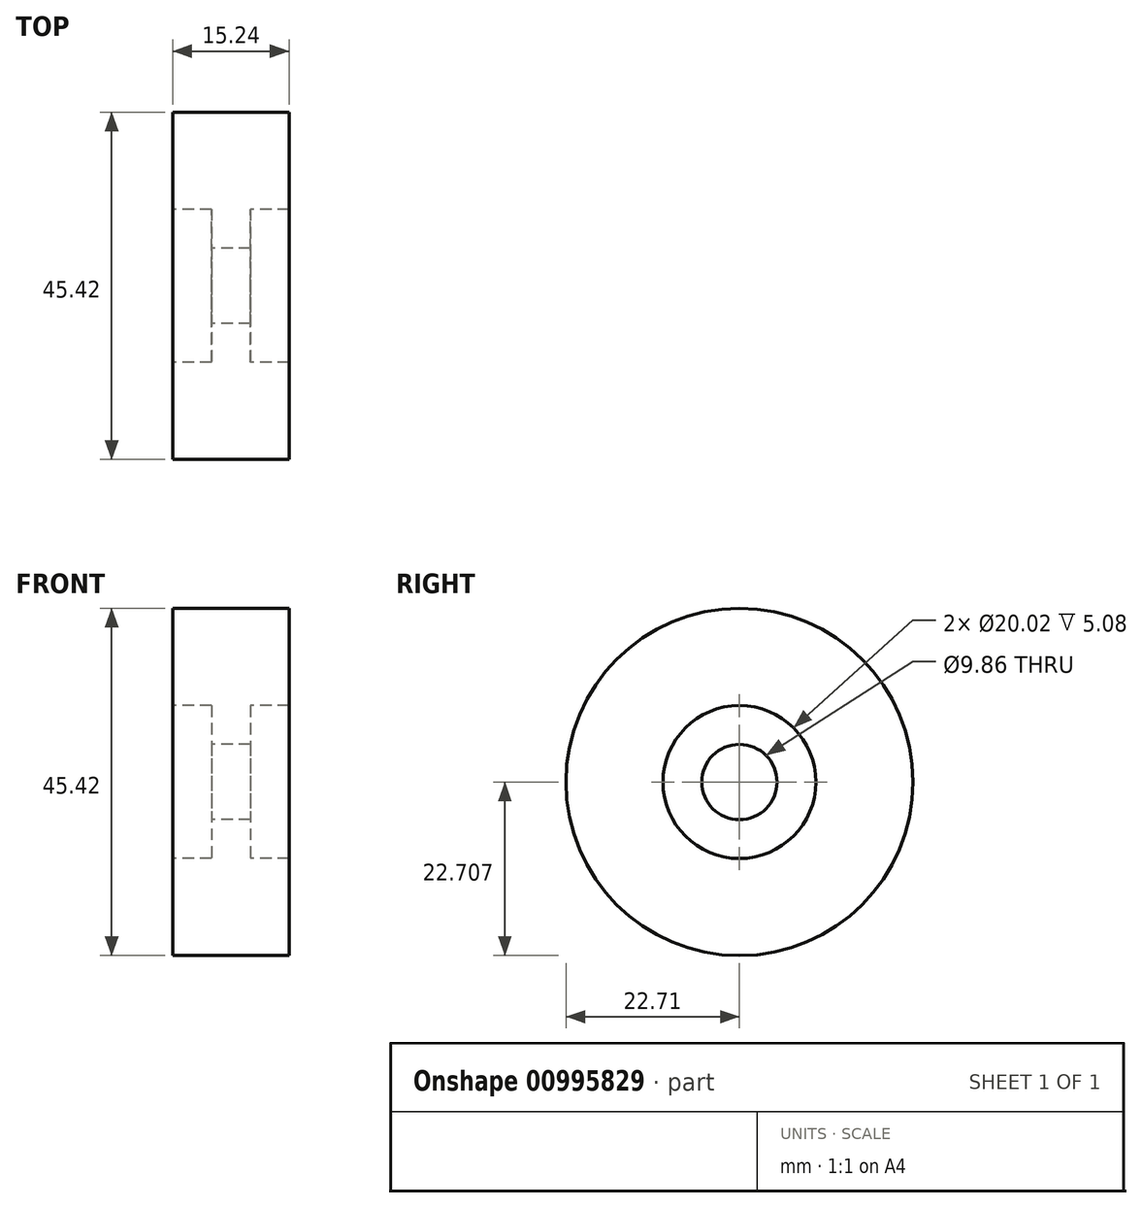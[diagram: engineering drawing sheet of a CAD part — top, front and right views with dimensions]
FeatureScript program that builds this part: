
annotation { "Feature Type Name" : "Feature", "Feature Type Description" : "" }
export const myFeature = defineFeature(function(context is Context, id is Id, definition is map)
    precondition{}
    {
        {
            var Q0;
            Q0=qCreatedBy(makeId("Front.planeOp"),FACE);
            var sketch = newSketch(context, id + "F0", { "sketchPlane" : qUnion([Q0])});
            skLineSegment(sketch, "E0", {"start": v(0, 7.87) * mm, "end": v(-5.08, 7.87) * mm});
            skLineSegment(sketch, "E1", {"start": v(-5.08, 7.87) * mm, "end": v(-5.08, 12.95) * mm});
            skLineSegment(sketch, "E2", {"start": v(-5.08, 12.95) * mm, "end": v(-10.16, 12.95) * mm});
            skLineSegment(sketch, "E3", {"start": v(-10.16, 12.95) * mm, "end": v(-10.16, 25.65) * mm});
            skLineSegment(sketch, "E4", {"start": v(-10.16, 25.65) * mm, "end": v(5.08, 25.65) * mm});
            skLineSegment(sketch, "E5", {"start": v(5.08, 25.65) * mm, "end": v(5.08, 12.95) * mm});
            skLineSegment(sketch, "E6", {"start": v(5.08, 12.95) * mm, "end": v(0, 12.95) * mm});
            skLineSegment(sketch, "E7", {"start": v(0, 12.95) * mm, "end": v(0, 7.87) * mm});
            skLineSegment(sketch, "E8", {"start": v(-5.08, 2.94) * mm, "end": v(0, 2.94) * mm});
            skSolve(sketch);
        }
        {
            var Q0;
            Q0=makeQuery(id+"F0.imprint","IMPRINT",FACE,{"disambiguationData":[TD([[makeQuery(id+"F0.imprint","IMPRINT",EDGE,{"derivedFrom":sQuery(id+"F0.wireOp",EDGE,"E0")}),-1.0]])]});
            var Q1;
            Q1=sQuery(id+"F0.wireOp",EDGE,"E8");
            revolve(context, id + "F1", {"surfaceOperationType" : NewSurfaceOperationType.NEW, "entities" : qUnion([Q0]), "axis" : qUnion([Q1]), "revolveType" : RevolveType.FULL});
        }
    });
